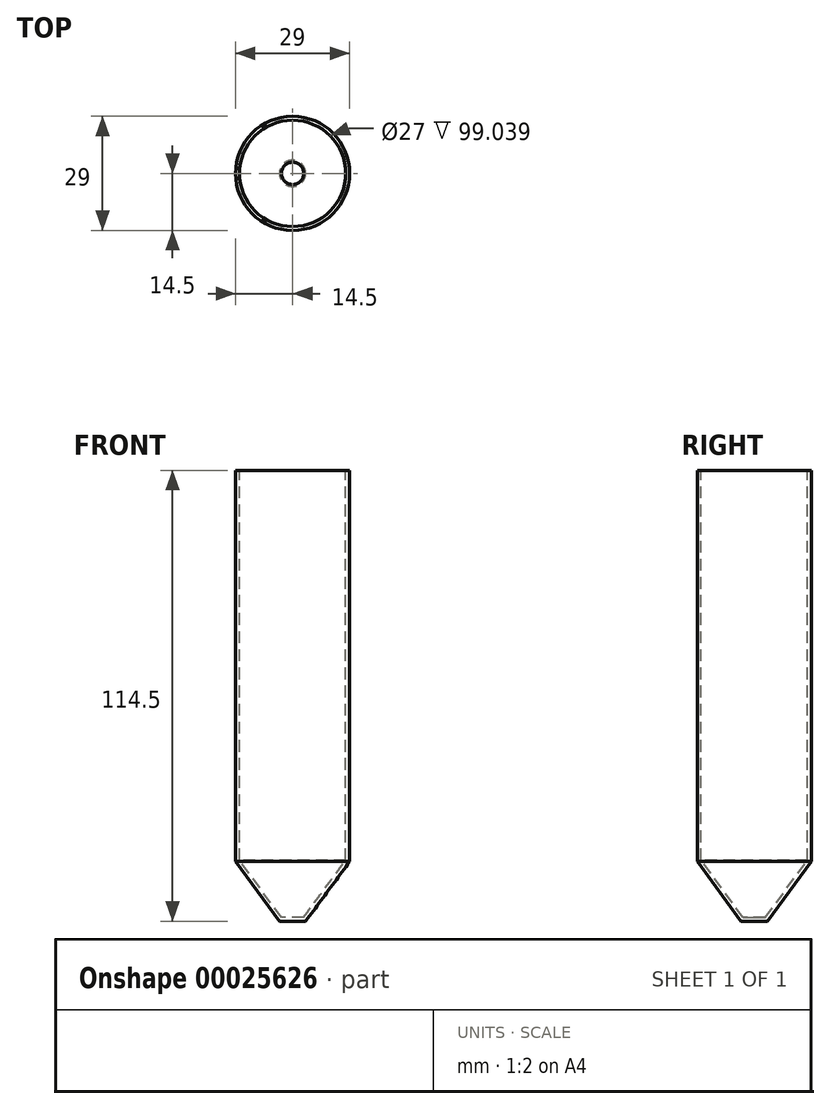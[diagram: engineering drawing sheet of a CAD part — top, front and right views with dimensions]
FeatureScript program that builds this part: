
annotation { "Feature Type Name" : "Feature", "Feature Type Description" : "" }
export const myFeature = defineFeature(function(context is Context, id is Id, definition is map)
    precondition{}
    {
        {
            var Q0;
            Q0=qCreatedBy(makeId("Front.planeOp"),FACE);
            var sketch = newSketch(context, id + "F0", { "sketchPlane" : qUnion([Q0])});
            skLineSegment(sketch, "E0.rect.bottom", {"start": v(3.34, -57.45) * mm, "end": v(0, -57.45) * mm});
            skLineSegment(sketch, "E0.rect.top", {"start": v(14.5, 57.05) * mm, "end": v(13.5, 57.05) * mm});
            skLineSegment(sketch, "E0.rect.left", {"start": v(14.5, -42.32) * mm, "end": v(14.5, 57.05) * mm});
            skPoint(sketch, "E0.rect.middle", {"position": v(0, 0) * mm});
            skLineSegment(sketch, "E1", {"start": v(14.5, -42.32) * mm, "end": v(3.34, -57.45) * mm});
            skLineSegment(sketch, "E2.0", {"start": v(13.5, -41.99) * mm, "end": v(13.5, 57.05) * mm});
            skLineSegment(sketch, "E2.1", {"start": v(13.5, -41.99) * mm, "end": v(2.84, -56.45) * mm});
            skLineSegment(sketch, "E2.2", {"start": v(2.84, -56.45) * mm, "end": v(0, -56.45) * mm});
            skLineSegment(sketch, "E3", {"start": v(0, -56.45) * mm, "end": v(0, -57.45) * mm});
            skSolve(sketch);
        }
        {
            var Q0;
            Q0=makeQuery(id+"F0.imprint","IMPRINT",FACE,{"disambiguationData":[TD([[makeQuery(id+"F0.imprint","IMPRINT",EDGE,{"derivedFrom":sQuery(id+"F0.wireOp",EDGE,"E0.rect.bottom")}),-1.0]])]});
            var Q1;
            Q1=sQuery(id+"F0.wireOp",EDGE,"E3");
            revolve(context, id + "F1", {"entities" : qUnion([Q0]), "axis" : qUnion([Q1]), "revolveType" : RevolveType.FULL});
        }
    });
